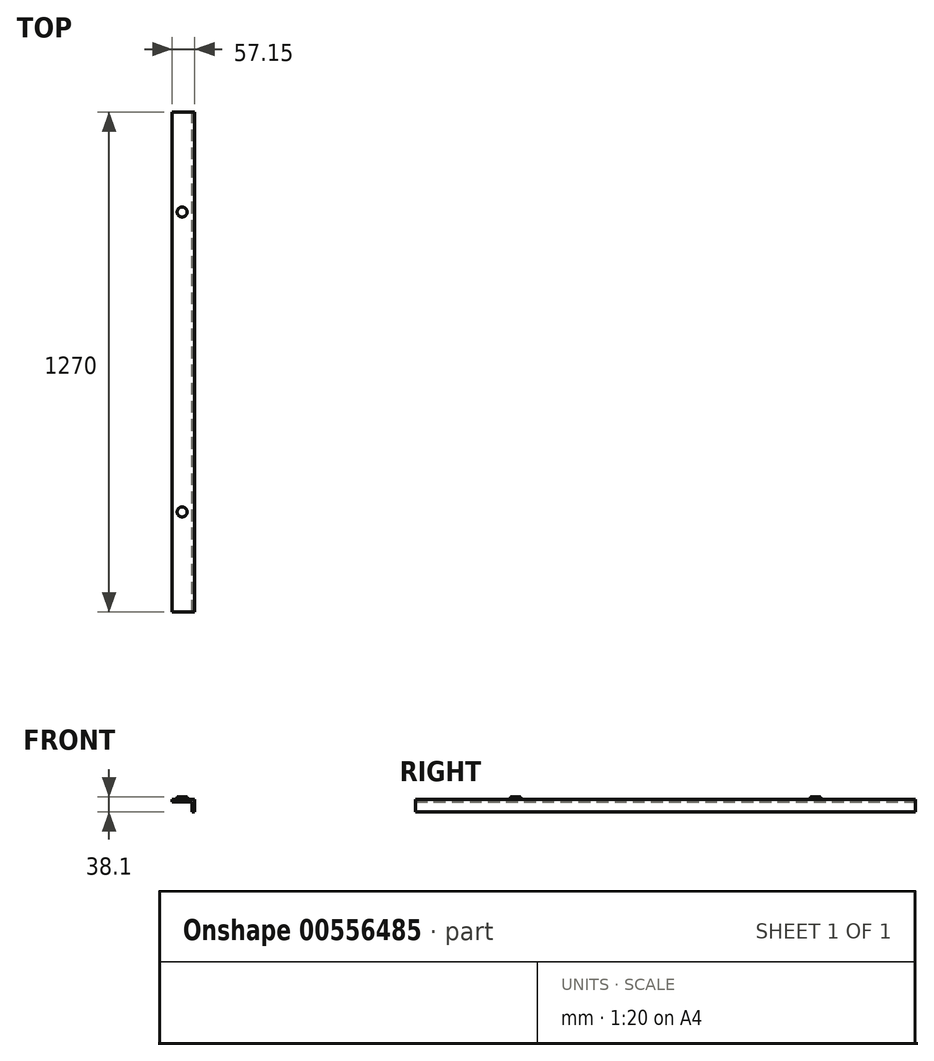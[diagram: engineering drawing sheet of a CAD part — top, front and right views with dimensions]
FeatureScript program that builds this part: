
annotation { "Feature Type Name" : "Feature", "Feature Type Description" : "" }
export const myFeature = defineFeature(function(context is Context, id is Id, definition is map)
    precondition{}
    {
        {
            var Q0;
            Q0=qCreatedBy(makeId("Front.planeOp"),FACE);
            var sketch = newSketch(context, id + "F0", { "sketchPlane" : qUnion([Q0])});
            skLineSegment(sketch, "E0", {"start": v(0, 0) * mm, "end": v(50.8, 0) * mm});
            skLineSegment(sketch, "E1", {"start": v(50.8, 0) * mm, "end": v(50.8, -25.4) * mm});
            skLineSegment(sketch, "E2.0", {"start": v(57.15, 6.35) * mm, "end": v(57.15, -25.4) * mm});
            skLineSegment(sketch, "E2.1", {"start": v(0, 6.35) * mm, "end": v(57.15, 6.35) * mm});
            skLineSegment(sketch, "E3", {"start": v(57.15, -25.4) * mm, "end": v(50.8, -25.4) * mm});
            skLineSegment(sketch, "E4", {"start": v(0, 6.35) * mm, "end": v(0, 0) * mm});
            skSolve(sketch);
        }
        {
            var Q0;
            Q0 = qSketchRegion(id + "F0", true);
            extrude(context, id + "F1", {"entities" : qUnion([Q0]), "endBound" : BoundingType.SYMMETRIC, "depth" : 1270 * mm, "offsetDistance" : 25.4 * mm});
        }
        {
            var Q0;
            Q0=qCreatedBy(makeId("Top.planeOp"),FACE);
            var sketch = newSketch(context, id + "F2", { "sketchPlane" : qUnion([Q0])});
            skCircle(sketch, "E5", {"center": v(25.4, 381) * mm, "radius": 12.7 * mm});
            skCircle(sketch, "E6", {"center": v(25.4, -381) * mm, "radius": 12.7 * mm});
            skSolve(sketch);
        }
        {
            var Q0;
            Q0 = qSketchRegion(id + "F2", true);
            extrude(context, id + "F3", {"entities" : qUnion([Q0]), "operationType" : NewBodyOperationType.ADD, "depth" : 12.7 * mm, "offsetDistance" : 25.4 * mm});
        }
        {
            var Q0;
            Q0=makeQuery(id+"F3.boolean.opBoolean","INTERSECT",EDGE,{"derivedFrom":[makeQuery(id+"F1.opExtrude","SWEPT_FACE",FACE,{"disambiguationData":[OSD([sQuery(id+"F0.wireOp",EDGE,"E2.1")])]}),makeQuery(id+"F3.opExtrude","SWEPT_FACE",FACE,{"disambiguationData":[OSD([sQuery(id+"F2.wireOp",EDGE,"E5")])]})]});
            fillet(context, id + "F4", {"entities" : qUnion([Q0]), "radius" : 7.62 * mm, "tangentPropagation" : true, "allowEdgeOverflow" : false});
        }
        {
            var Q0;
            Q0=makeQuery(id+"F3.boolean.opBoolean","INTERSECT",EDGE,{"derivedFrom":[makeQuery(id+"F1.opExtrude","SWEPT_FACE",FACE,{"disambiguationData":[OSD([sQuery(id+"F0.wireOp",EDGE,"E2.1")])]}),makeQuery(id+"F3.opExtrude","SWEPT_FACE",FACE,{"disambiguationData":[OSD([sQuery(id+"F2.wireOp",EDGE,"E6")])]})]});
            fillet(context, id + "F5", {"entities" : qUnion([Q0]), "radius" : 7.62 * mm, "tangentPropagation" : true, "allowEdgeOverflow" : false});
        }
    });
